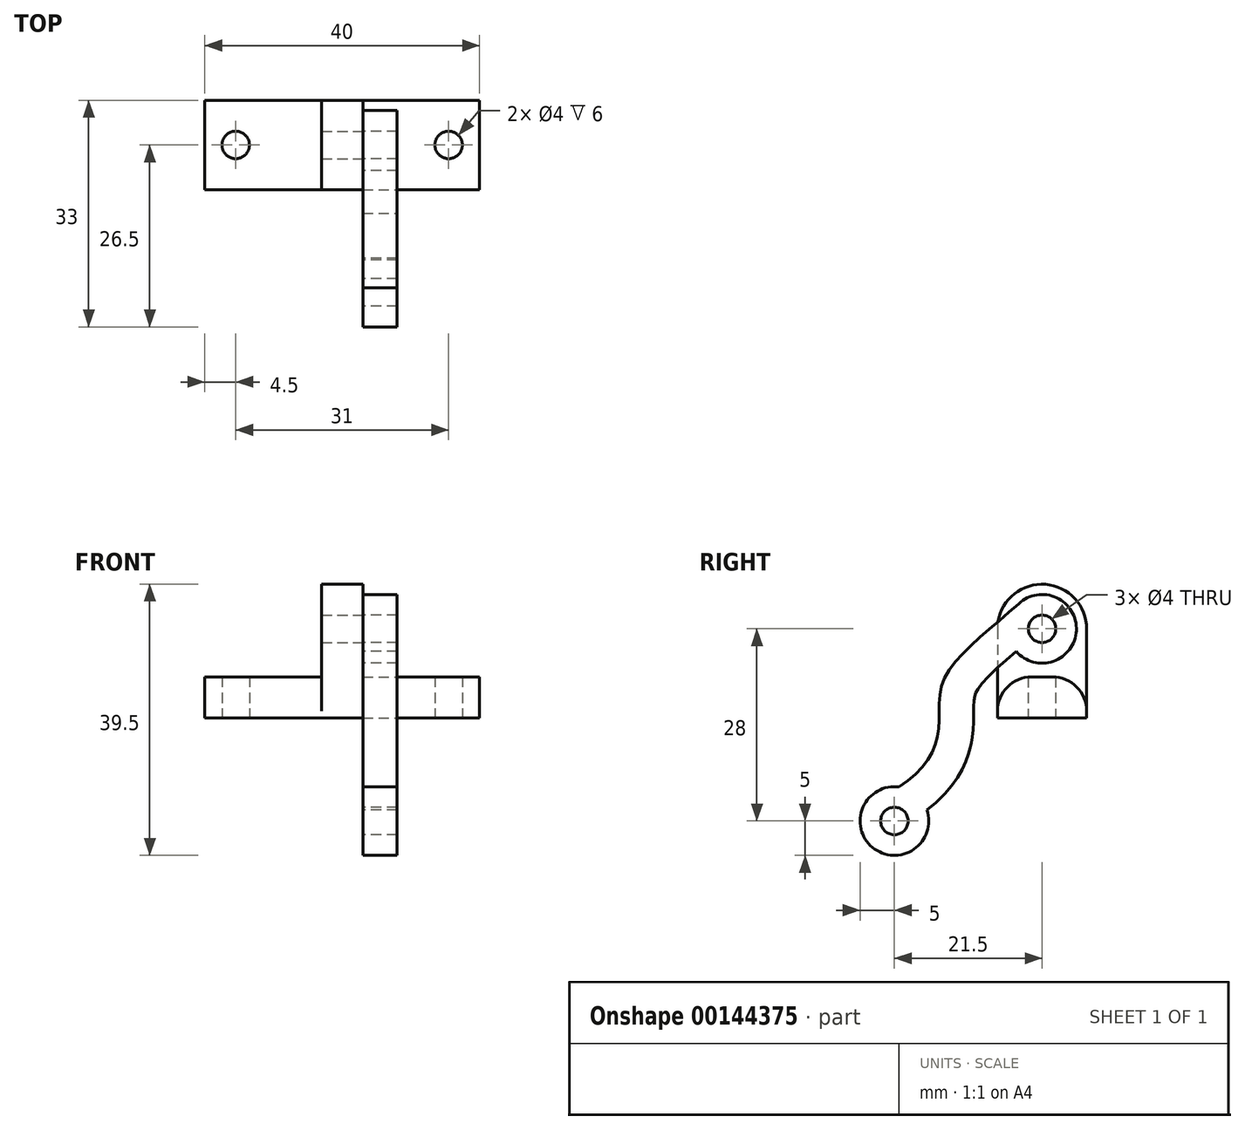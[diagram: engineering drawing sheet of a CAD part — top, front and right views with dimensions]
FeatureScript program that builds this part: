
annotation { "Feature Type Name" : "Feature", "Feature Type Description" : "" }
export const myFeature = defineFeature(function(context is Context, id is Id, definition is map)
    precondition{}
    {
        {
            var Q0;
            Q0=qCreatedBy(makeId("Top.planeOp"),FACE);
            var sketch = newSketch(context, id + "F0", { "sketchPlane" : qUnion([Q0])});
            skPoint(sketch, "E0", {"position": v(-15.5, 25) * mm});
            skPoint(sketch, "E1", {"position": v(15.5, 25) * mm});
            skLineSegment(sketch, "E2.bottom", {"start": v(-20, 38) * mm, "end": v(20, 38) * mm});
            skLineSegment(sketch, "E2.top", {"start": v(-20, 25) * mm, "end": v(-15.5, 25) * mm});
            skLineSegment(sketch, "E2.left", {"start": v(-20, 38) * mm, "end": v(-20, 25) * mm});
            skLineSegment(sketch, "E2.right", {"start": v(20, 38) * mm, "end": v(20, 25) * mm});
            skLineSegment(sketch, "E3", {"start": v(15.5, 25) * mm, "end": v(20, 25) * mm});
            skLineSegment(sketch, "E4", {"start": v(-15.5, 25) * mm, "end": v(15.5, 25) * mm});
            skPoint(sketch, "E5", {"position": v(-15.5, 31.5) * mm});
            skLineSegment(sketch, "E6", {"start": v(-15.5, 25) * mm, "end": v(-15.5, 38) * mm, "construction": true});
            skPoint(sketch, "E7.MirrorP", {"position": v(15.5, 31.5) * mm});
            skSolve(sketch);
        }
        {
            var Q0;
            Q0=makeQuery(id+"F0.imprint","IMPRINT",FACE,{"disambiguationData":[TD([[makeQuery(id+"F0.imprint","IMPRINT",EDGE,{"derivedFrom":sQuery(id+"F0.wireOp",EDGE,"E2.bottom")}),-1.0]])]});
            extrude(context, id + "F1", {"entities" : qUnion([Q0]), "depth" : 6 * mm});
        }
        {
            var Q0;
            Q0=sQuery(id+"F0.wireOp",VERTEX,"E5");
            var Q1;
            Q1=sQuery(id+"F0.wireOp",VERTEX,"E7.MirrorP");
            var Q2;
            Q2=makeQuery(id+"F1.opExtrude","SWEPT_BODY",BODY,{"disambiguationData":[OSD([sQuery(id+"F0.wireOp",EDGE,"E2.bottom"),sQuery(id+"F0.wireOp",EDGE,"E2.top"),sQuery(id+"F0.wireOp",EDGE,"E2.left"),sQuery(id+"F0.wireOp",EDGE,"E2.right"),sQuery(id+"F0.wireOp",EDGE,"E3"),sQuery(id+"F0.wireOp",EDGE,"E4")])]});
            hole(context, id + "F2", {"style" : HoleStyle.SIMPLE, "endStyle" : HoleEndStyle.THROUGH, "oppositeDirection" : true, "holeDiameter" : 4 * mm, "locations" : qUnion([Q0, Q1]), "scope" : qUnion([Q2]), "isTappedThrough" : true});
        }
        {
            var Q0;
            Q0=makeQuery(id+"F1.opExtrude","CAP_EDGE",EDGE,{"disambiguationData":[OSD([sQuery(id+"F0.wireOp",EDGE,"E2.bottom")])],"isStart":false});
            var Q1;
            Q1=makeQuery(id+"F1.opExtrude","CAP_EDGE",EDGE,{"disambiguationData":[OSD([sQuery(id+"F0.wireOp",EDGE,"E2.top"),sQuery(id+"F0.wireOp",EDGE,"E3"),sQuery(id+"F0.wireOp",EDGE,"E4")])],"isStart":false});
            fillet(context, id + "F3", {"entities" : qUnion([Q0, Q1]), "radius" : 5 * mm, "tangentPropagation" : true, "allowEdgeOverflow" : false});
        }
        {
            var Q0;
            Q0=qCreatedBy(makeId("Right.planeOp"),FACE);
            var sketch = newSketch(context, id + "F4", { "sketchPlane" : qUnion([Q0])});
            skLineSegment(sketch, "E8.0.0", {"start": v(33, 6) * mm, "end": v(30, 6) * mm});
            skArc(sketch, "E8.0.1", {"start": v(30, 6) * mm, "mid": v(26.46, 4.54) * mm, "end": v(25, 1) * mm});
            skLineSegment(sketch, "E8.0.2", {"start": v(25, 1) * mm, "end": v(25, 0) * mm});
            skLineSegment(sketch, "E8.0.3", {"start": v(25, 0) * mm, "end": v(38, 0) * mm});
            skLineSegment(sketch, "E8.0.4", {"start": v(38, 0) * mm, "end": v(38, 1) * mm});
            skArc(sketch, "E8.0.5", {"start": v(38, 1) * mm, "mid": v(36.54, 4.54) * mm, "end": v(33, 6) * mm});
            skLineSegment(sketch, "E9", {"start": v(25, 1) * mm, "end": v(25, 13) * mm});
            skLineSegment(sketch, "E10", {"start": v(38, 1) * mm, "end": v(38, 13) * mm});
            skArc(sketch, "E11", {"start": v(38, 13) * mm, "mid": v(31.5, 19.5) * mm, "end": v(25, 13) * mm});
            skSolve(sketch);
        }
        {
            var Q0;
            Q0 = qSketchRegion(id + "F4", true);
            extrude(context, id + "F5", {"entities" : qUnion([Q0]), "operationType" : NewBodyOperationType.ADD, "endBound" : BoundingType.SYMMETRIC, "depth" : 6 * mm});
        }
        {
            var Q0;
            Q0=sQuery(id+"F4.wireOp",VERTEX,"E11.center");
            var Q1;
            Q1=makeQuery(id+"F1.opExtrude","SWEPT_BODY",BODY,{"disambiguationData":[OSD([sQuery(id+"F0.wireOp",EDGE,"E2.bottom"),sQuery(id+"F0.wireOp",EDGE,"E2.top"),sQuery(id+"F0.wireOp",EDGE,"E2.left"),sQuery(id+"F0.wireOp",EDGE,"E2.right"),sQuery(id+"F0.wireOp",EDGE,"E3"),sQuery(id+"F0.wireOp",EDGE,"E4")])]});
            hole(context, id + "F6", {"style" : HoleStyle.SIMPLE, "endStyle" : HoleEndStyle.BLIND, "holeDiameter" : 4 * mm, "holeDepth" : 25 * mm, "locations" : qUnion([Q0]), "scope" : qUnion([Q1])});
        }
        {
            var Q0;
            Q0=sQuery(id+"F4.wireOp",VERTEX,"E11.center");
            var Q1;
            Q1=makeQuery(id+"F1.opExtrude","SWEPT_BODY",BODY,{"disambiguationData":[OSD([sQuery(id+"F0.wireOp",EDGE,"E2.bottom"),sQuery(id+"F0.wireOp",EDGE,"E2.top"),sQuery(id+"F0.wireOp",EDGE,"E2.left"),sQuery(id+"F0.wireOp",EDGE,"E2.right"),sQuery(id+"F0.wireOp",EDGE,"E3"),sQuery(id+"F0.wireOp",EDGE,"E4")])]});
            hole(context, id + "F7", {"style" : HoleStyle.SIMPLE, "endStyle" : HoleEndStyle.BLIND, "oppositeDirection" : true, "holeDiameter" : 4 * mm, "holeDepth" : 25 * mm, "locations" : qUnion([Q0]), "scope" : qUnion([Q1])});
        }
        {
            var Q0;
            Q0=makeQuery(id+"F5.opExtrude","CAP_FACE",FACE,{"disambiguationData":[OSD([sQuery(id+"F4.wireOp",EDGE,"E8.0.2"),sQuery(id+"F4.wireOp",EDGE,"E8.0.3"),sQuery(id+"F4.wireOp",EDGE,"E8.0.4"),sQuery(id+"F4.wireOp",EDGE,"E9"),sQuery(id+"F4.wireOp",EDGE,"E10"),sQuery(id+"F4.wireOp",EDGE,"E11")])],"isStart":false});
            var sketch = newSketch(context, id + "F8", { "sketchPlane" : qUnion([Q0])});
            skPoint(sketch, "E12", {"position": v(10, -15) * mm});
            skCircle(sketch, "E13", {"center": v(10, -15) * mm, "radius": 5 * mm});
            skCircle(sketch, "E14", {"center": v(31.5, 13) * mm, "radius": 5 * mm});
            skFitSpline(sketch, "E15", {"points": [v(28.1, 16.67) * mm, v(17.2, 5.55) * mm, v(16.32, -2.54) * mm, v(10.7, -10.05) * mm], "startDerivative": vector(-31.73, -29.29) * mm, "endDerivative": vector(-30.96, -20.05) * mm});
            skFitSpline(sketch, "E16.0", {"points": [v(31.51, 12.99) * mm, v(30.8, 12.32) * mm, v(29.34, 11.05) * mm, v(27.24, 9.27) * mm, v(25.33, 7.62) * mm, v(23.71, 6.11) * mm, v(22.72, 5) * mm, v(22.25, 4.37) * mm, v(22.05, 4.06) * mm, v(21.94, 3.86) * mm, v(21.85, 3.69) * mm, v(21.8, 3.56) * mm, v(21.75, 3.42) * mm, v(21.68, 3.2) * mm, v(21.62, 2.89) * mm, v(21.56, 2.39) * mm, v(21.53, 1.76) * mm, v(21.53, 1) * mm, v(21.53, 0.1) * mm, v(21.52, -0.91) * mm, v(21.47, -1.87) * mm, v(21.38, -2.7) * mm, v(21.3, -3.24) * mm, v(21.21, -3.7) * mm, v(21.12, -4.13) * mm, v(20.98, -4.68) * mm, v(20.78, -5.33) * mm, v(20.47, -6.19) * mm, v(20.01, -7.22) * mm, v(19.35, -8.41) * mm, v(18.58, -9.54) * mm, v(17.43, -10.97) * mm, v(15.77, -12.6) * mm, v(14.24, -13.73) * mm, v(13.42, -14.26) * mm]});
            skSolve(sketch);
        }
        {
            var Q0;
            {var subQ0=sQuery(id+"F8.wireOp",EDGE,"E14");var subQ1=makeQuery(id+"F8.imprint","INTERSECT",VERTEX,{"derivedFrom":[subQ0,sQuery(id+"F8.wireOp",EDGE,"E15")]});Q0=makeQuery(id+"F8.imprint","IMPRINT",FACE,{"disambiguationData":[TD([[makeQuery(id+"F8.imprint","IMPRINT",EDGE,{"disambiguationData":[TD([[subQ1,-1.0]])],"derivedFrom":subQ0}),1.0]])]});}
            var Q1;
            {var subQ3=sQuery(id+"F8.wireOp",EDGE,"E15");var subQ6=sQuery(id+"F8.wireOp",EDGE,"E14");var subQ9=makeQuery(id+"F8.imprint","INTERSECT",VERTEX,{"derivedFrom":[subQ6,subQ3]});Q1=makeQuery(id+"F8.imprint","IMPRINT",FACE,{"disambiguationData":[TD([[makeQuery(id+"F8.imprint","IMPRINT",EDGE,{"disambiguationData":[TD([[subQ9,-1.0]])],"derivedFrom":subQ6}),-1.0]])]});}
            var Q2;
            {var subQ3=sQuery(id+"F8.wireOp",EDGE,"E15");var subQ5=sQuery(id+"F8.wireOp",EDGE,"E13");var subQ6=makeQuery(id+"F8.imprint","INTERSECT",VERTEX,{"derivedFrom":[subQ5,subQ3]});Q2=makeQuery(id+"F8.imprint","IMPRINT",FACE,{"disambiguationData":[TD([[makeQuery(id+"F8.imprint","IMPRINT",EDGE,{"disambiguationData":[TD([[subQ6,1.0]])],"derivedFrom":subQ5}),-1.0]])]});}
            var Q3;
            {var subQ0=sQuery(id+"F8.wireOp",EDGE,"E13");var subQ1=makeQuery(id+"F8.imprint","INTERSECT",VERTEX,{"derivedFrom":[subQ0,sQuery(id+"F8.wireOp",EDGE,"E15")]});Q3=makeQuery(id+"F8.imprint","IMPRINT",FACE,{"disambiguationData":[TD([[makeQuery(id+"F8.imprint","IMPRINT",EDGE,{"disambiguationData":[TD([[subQ1,1.0]])],"derivedFrom":subQ0}),1.0]])]});}
            extrude(context, id + "F9", {"entities" : qUnion([Q0, Q1, Q2, Q3]), "depth" : 5 * mm});
        }
        {
            var Q0;
            Q0=sQuery(id+"F8.wireOp",VERTEX,"E13.center");
            var Q1;
            Q1=makeQuery(id+"F1.opExtrude","SWEPT_BODY",BODY,{"disambiguationData":[OSD([sQuery(id+"F0.wireOp",EDGE,"E2.bottom"),sQuery(id+"F0.wireOp",EDGE,"E2.top"),sQuery(id+"F0.wireOp",EDGE,"E2.left"),sQuery(id+"F0.wireOp",EDGE,"E2.right"),sQuery(id+"F0.wireOp",EDGE,"E3"),sQuery(id+"F0.wireOp",EDGE,"E4")])]});
            var Q2;
            Q2=makeQuery(id+"F9.opExtrude","SWEPT_BODY",BODY,{"disambiguationData":[OSD([sQuery(id+"F4.wireOp",EDGE,"E8.0.2"),sQuery(id+"F4.wireOp",EDGE,"E8.0.3"),sQuery(id+"F4.wireOp",EDGE,"E8.0.4"),sQuery(id+"F4.wireOp",EDGE,"E9"),sQuery(id+"F4.wireOp",EDGE,"E10"),sQuery(id+"F4.wireOp",EDGE,"E11"),sQuery(id+"F7.hole-0.sketch.wireOp",EDGE,"core_line_2"),sQuery(id+"F8.wireOp",EDGE,"E13"),sQuery(id+"F8.wireOp",EDGE,"E14"),sQuery(id+"F8.wireOp",EDGE,"E15"),sQuery(id+"F8.wireOp",EDGE,"E16.0")])]});
            hole(context, id + "F10", {"style" : HoleStyle.SIMPLE, "endStyle" : HoleEndStyle.BLIND, "oppositeDirection" : true, "holeDiameter" : 4 * mm, "holeDepth" : 25 * mm, "locations" : qUnion([Q0]), "scope" : qUnion([Q1, Q2])});
        }
    });
